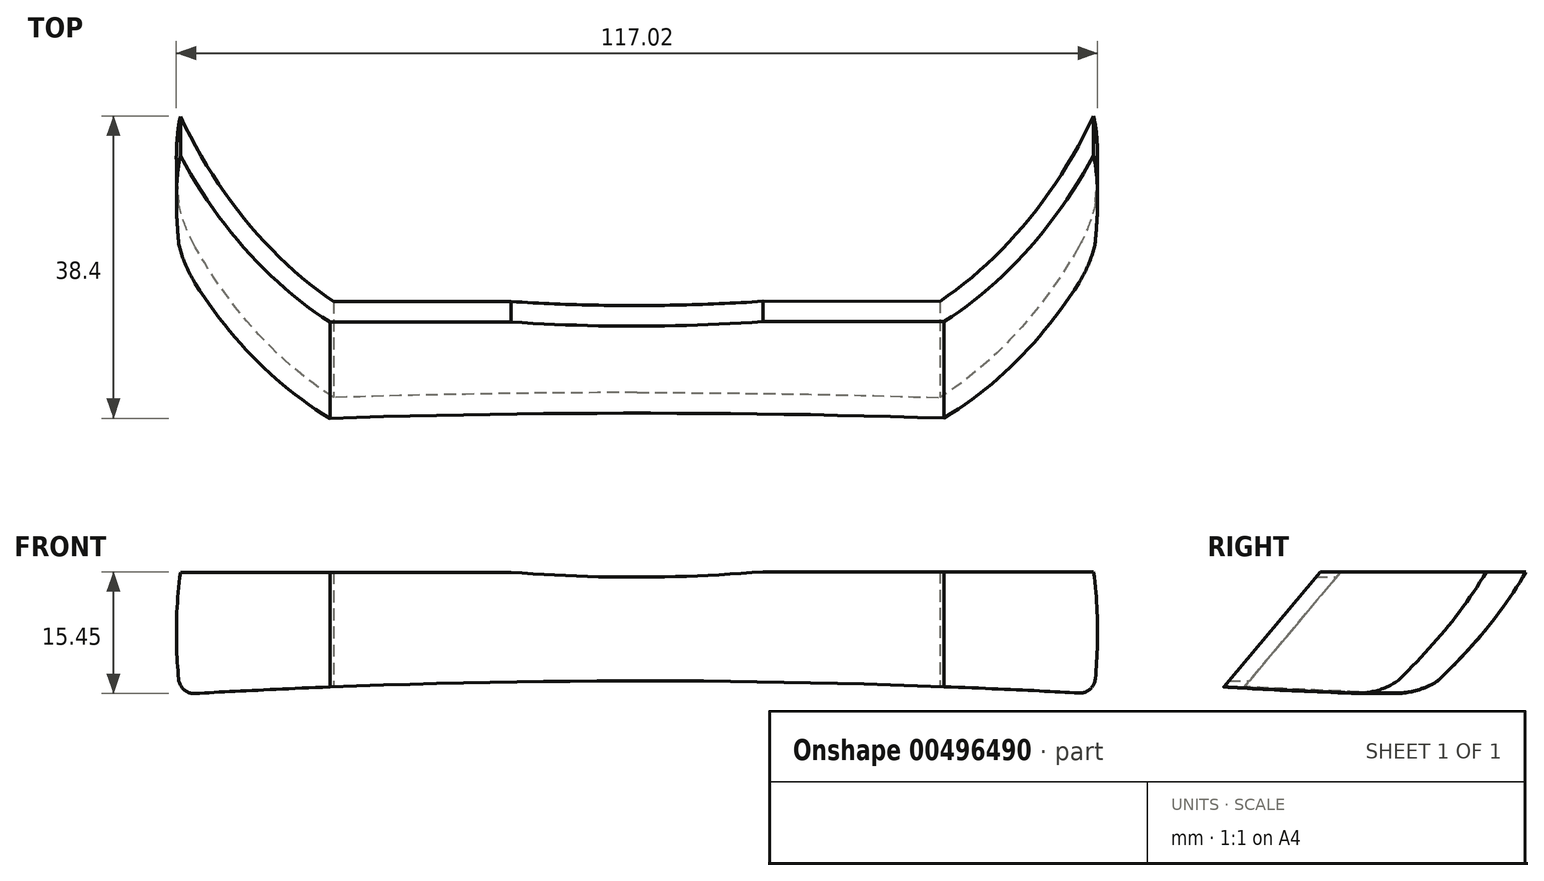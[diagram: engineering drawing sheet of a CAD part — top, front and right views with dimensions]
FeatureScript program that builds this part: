
annotation { "Feature Type Name" : "Feature", "Feature Type Description" : "" }
export const myFeature = defineFeature(function(context is Context, id is Id, definition is map)
    precondition{}
    {
        {
            var Q0;
            Q0=qCreatedBy(makeId("Front.planeOp"),FACE);
            var sketch = newSketch(context, id + "F0", { "sketchPlane" : qUnion([Q0])});
            skArc(sketch, "E0", {"start": v(-58, 15.5) * mm, "mid": v(-58.5, 7.75) * mm, "end": v(-58, 0) * mm});
            skArc(sketch, "E1", {"start": v(58, 0.06) * mm, "mid": v(58.5, 7.8) * mm, "end": v(58, 15.56) * mm});
            skArc(sketch, "E2", {"start": v(58, 0.06) * mm, "mid": v(0, 1.71) * mm, "end": v(-58, 0) * mm});
            skLineSegment(sketch, "E3", {"start": v(-58, 15.5) * mm, "end": v(-16, 15.5) * mm});
            skLineSegment(sketch, "E4", {"start": v(58, 15.56) * mm, "end": v(16, 15.56) * mm});
            skArc(sketch, "E5", {"start": v(-16, 15.5) * mm, "mid": v(0, 14.89) * mm, "end": v(16, 15.56) * mm});
            skSolve(sketch);
        }
        {
            var Q0;
            Q0=makeQuery(id+"F0.imprint","IMPRINT",FACE,{"disambiguationData":[TD([[makeQuery(id+"F0.imprint","IMPRINT",EDGE,{"derivedFrom":sQuery(id+"F0.wireOp",EDGE,"E0")}),1.0]])]});
            var Q1;
            Q1=sQuery(id+"F0.wireOp",EDGE,"E0");
            var Q2;
            Q2=sQuery(id+"F0.wireOp",EDGE,"170cc053-ae22-420d-94f3-23036fa35352");
            var Q3;
            Q3=sQuery(id+"F0.wireOp",EDGE,"0ddac671-3e88-4b45-b8af-5c0815418419");
            var Q4;
            Q4=sQuery(id+"F0.wireOp",EDGE,"3fd53242-a7d9-4184-a239-63e3792486e1");
            var Q5;
            Q5=sQuery(id+"F0.wireOp",EDGE,"E1");
            var Q6;
            Q6=sQuery(id+"F0.wireOp",EDGE,"0a818849-f8e2-4715-b427-94ae307ff970");
            extrude(context, id + "F1", {"entities" : qUnion([Q0]), "surfaceEntities" : qUnion([Q1, Q2, Q3, Q4, Q5, Q6]), "depth" : 40 * mm, "hasSecondDirection" : true, "secondDirectionOppositeDirection" : true, "secondDirectionDepth" : 11 * mm});
        }
        {
            var Q0;
            Q0=makeQuery(id+"F1.opExtrude","CAP_FACE",FACE,{"disambiguationData":[OSD([sQuery(id+"F0.wireOp",EDGE,"E0"),sQuery(id+"F0.wireOp",EDGE,"E1"),sQuery(id+"F0.wireOp",EDGE,"E2"),sQuery(id+"F0.wireOp",EDGE,"E3"),sQuery(id+"F0.wireOp",EDGE,"E4"),sQuery(id+"F0.wireOp",EDGE,"E5")])],"isStart":false});
            var Q1;
            Q1=makeQuery(id+"F1.opExtrude","CAP_EDGE",EDGE,{"disambiguationData":[OSD([sQuery(id+"F0.wireOp",EDGE,"E4")])],"isStart":false});
            cPlane(context, id + "F2", {"entities" : qUnion([Q0, Q1]), "cplaneType" : CPlaneType.LINE_ANGLE, "offset" : 25 * mm, "angle" : 130 * degree, "width" : 150 * mm, "height" : 150 * mm});
        }
        {
            var Q0;
            Q0=qCreatedBy(id+"F2.planeOp",FACE);
            var sketch = newSketch(context, id + "F3", { "sketchPlane" : qUnion([Q0])});
            skLineSegment(sketch, "E6", {"start": v(61, 22.98) * mm, "end": v(61, 1.98) * mm});
            skLineSegment(sketch, "E7", {"start": v(-61, 22.98) * mm, "end": v(-61, 1.98) * mm});
            skArc(sketch, "E8", {"start": v(61, 1.98) * mm, "mid": v(51.64, 14.2) * mm, "end": v(39, 22.98) * mm});
            skArc(sketch, "E9", {"start": v(-39, 22.98) * mm, "mid": v(-51.64, 14.2) * mm, "end": v(-61, 1.98) * mm});
            skLineSegment(sketch, "E10", {"start": v(0, 20.98) * mm, "end": v(38.5, 21) * mm});
            skLineSegment(sketch, "E11", {"start": v(0, 20.98) * mm, "end": v(-38.53, 20.98) * mm});
            skArc(sketch, "E12", {"start": v(-38.53, 20.98) * mm, "mid": v(-52.62, 10.12) * mm, "end": v(-62, -4.98) * mm});
            skArc(sketch, "E13", {"start": v(61.99, -4.94) * mm, "mid": v(52.59, 10.15) * mm, "end": v(38.5, 21) * mm});
            skLineSegment(sketch, "E14", {"start": v(59.42, -21.7) * mm, "end": v(60.21, -21.7) * mm});
            skPoint(sketch, "E15.start.orphan", {"position": v(38.5, 0) * mm});
            skPoint(sketch, "E16.start.orphan", {"position": v(-38.53, 0) * mm});
            skLineSegment(sketch, "E17", {"start": v(61, 22.98) * mm, "end": v(61, 52.98) * mm});
            skLineSegment(sketch, "E18", {"start": v(-61, 22.98) * mm, "end": v(-61, 52.98) * mm});
            skLineSegment(sketch, "E19", {"start": v(61, 52.98) * mm, "end": v(-61, 52.98) * mm});
            skLineSegment(sketch, "E20", {"start": v(39, 22.98) * mm, "end": v(-39, 22.98) * mm});
            skLineSegment(sketch, "E21", {"start": v(0, -28.22) * mm, "end": v(61, -28.22) * mm});
            skLineSegment(sketch, "E22", {"start": v(0, -28.22) * mm, "end": v(-61, -28.22) * mm});
            skLineSegment(sketch, "E23", {"start": v(-61, -28.22) * mm, "end": v(-61, -10.63) * mm});
            skLineSegment(sketch, "E24", {"start": v(61, -28.22) * mm, "end": v(61, -12.47) * mm});
            skLineSegment(sketch, "E25", {"start": v(61, -12.47) * mm, "end": v(61, -2.63) * mm});
            skLineSegment(sketch, "E26", {"start": v(-61, -10.63) * mm, "end": v(-61, -2.63) * mm});
            skSolve(sketch);
        }
        {
            var Q0;
            Q0=makeQuery(id+"F3.imprint","IMPRINT",FACE,{"disambiguationData":[TD([[makeQuery(id+"F3.imprint","IMPRINT",EDGE,{"derivedFrom":sQuery(id+"F3.wireOp",EDGE,"E10")}),-1.0]])]});
            var Q1;
            Q1=makeQuery(id+"F3.imprint","IMPRINT",FACE,{"disambiguationData":[TD([[makeQuery(id+"F3.imprint","IMPRINT",EDGE,{"derivedFrom":sQuery(id+"F3.wireOp",EDGE,"E6")}),-1.0]])]});
            extrude(context, id + "F4", {"entities" : qUnion([Q0, Q1]), "operationType" : NewBodyOperationType.REMOVE, "oppositeDirection" : true, "depth" : 35 * mm, "hasSecondDirection" : true, "secondDirectionOppositeDirection" : false, "secondDirectionDepth" : 27.9 * mm});
        }
        {
            var Q0;
            Q0=makeQuery(id+"F1.opExtrude","SWEPT_EDGE",EDGE,{"disambiguationData":[OSD([sQuery(id+"F0.wireOp",EDGE,"E1"),sQuery(id+"F0.wireOp",EDGE,"E2")])]});
            var Q1;
            Q1=makeQuery(id+"F1.opExtrude","SWEPT_EDGE",EDGE,{"disambiguationData":[OSD([sQuery(id+"F0.wireOp",EDGE,"E0"),sQuery(id+"F0.wireOp",EDGE,"E2")])]});
            fillet(context, id + "F5", {"entities" : qUnion([Q0, Q1]), "radius" : 2 * mm, "tangentPropagation" : true, "allowEdgeOverflow" : false});
        }
    });
